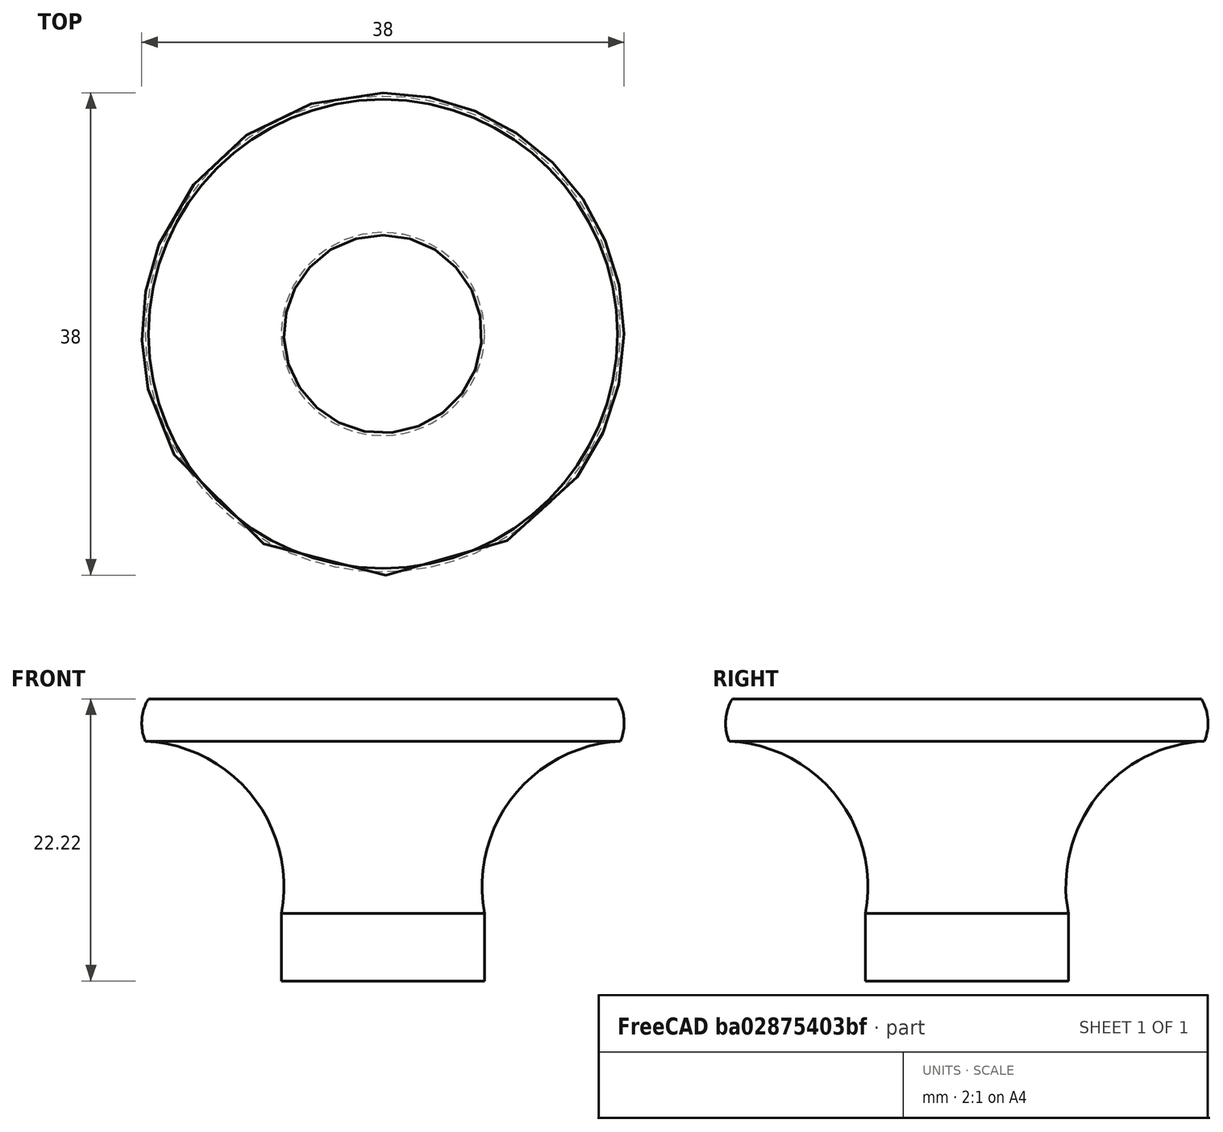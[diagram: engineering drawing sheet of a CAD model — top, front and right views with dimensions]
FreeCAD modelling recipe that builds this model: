
FCSTD DOCUMENT  (FreeCAD 1.1R20260325 (Git shallow))
Label: msf068
License: All rights reserved
LicenseURL: https://en.wikipedia.org/wiki/All_rights_reserved
objects: App::LinkGroup×2, App::Point×2, Sketcher::SketchObject×1, PartDesign::Revolution×1, PartDesign::Body×1, App::Part×1
note: 6 computed .brp shape members not serialized (recipe doc carries the construction recipe); baked Part::Feature solids carry a one-line shape summary decoded from their .brp

FEATURE [Sketcher::SketchObject] Sketch
  ArcFitTolerance = 0
  ExternalTypes = [0]
  FullyConstrained = false
  MakeInternals = false
  MapMode = 5
  Placement = pos=(0,0,0) rot=(0.57735,0.57735,0.57735;2.0944rad)
  _ExternalGeoVersion = 0
  sketch-geometry (8):
    g0: LineSegment StartX=0 StartY=0 StartZ=0 EndX=8 EndY=0 EndZ=0
    g1: LineSegment StartX=8 StartY=0 StartZ=0 EndX=8 EndY=5.33538 EndZ=0
    g2: ArcOfCircle CenterX=19.2411 CenterY=7.45526 CenterZ=0 NormalX=0 NormalY=0 NormalZ=1 AngleXU=0 Radius=11.4392 StartAngle=1.61634 EndAngle=3.32799
    g3: ArcOfCircle CenterX=15.253 CenterY=20.3071 CenterZ=0 NormalX=0 NormalY=0 NormalZ=1 AngleXU=0 Radius=3.74848 StartAngle=5.89336 EndAngle=6.82
    g4: ArcOfCircle CenterX=-1.25475 CenterY=-61.8052 CenterZ=0 NormalX=0 NormalY=0 NormalZ=1 AngleXU=0 Radius=86.3143 StartAngle=1.34019 EndAngle=1.55626
    g5: LineSegment StartX=4.2e-15 StartY=24.5 StartZ=0 EndX=0 EndY=0 EndZ=0
    g6: LineSegment [constr] StartX=19 StartY=0 StartZ=0 EndX=19 EndY=20.4133 EndZ=0
    g7: LineSegment [constr] StartX=4.2e-15 StartY=24.5 StartZ=0 EndX=9.88874e-07 EndY=24.5 EndZ=0
  constraints (17):
    c: Coincident(g0,g-1)
    c: PointOnObject(g0,g-1)
    c: Coincident(g1,g0)
    c: Vertical(g1)
    c: Coincident(g2,g1)
    c: Coincident(g3,g2)
    c: Coincident(g4,g3)
    c: PointOnObject(g4,g-2)
    c: Coincident(g5,g4)
    c: Coincident(g5,g0)
    c: DistanceX(g0,g0) = 8
    c: PointOnObject(g6,g-1)
    c: Vertical(g6)
    c: PointOnObject(g6,g3)
    c: DistanceX(g4,g6) = 19
    c: DistanceY(g0,g7) = 24.5
    c: Tangent(g4,g7) = 1.5708
FEATURE [PartDesign::Revolution] Revolution
  Angle = 360
  Angle2 = 0
  Axis = (1e-16,-1e-16,1)
  Base = (0,0,0)
  FuseOrder = 0
  Placement = pos=(0,0,0) rot=(0.57735,0.57735,0.57735;2.0944rad)
  Profile = -> Sketch
  ReferenceAxis = -> Sketch [V_Axis]
  Reversed = true
  Suppressed = false
  Type = 0
FEATURE [PartDesign::Body] Body
  AllowCompound = true
  Group = -> [Sketch,Revolution]
  Origin = -> Origin001
  Tip = -> Revolution
FEATURE [App::Part] Part
  Group = -> [Body]
  Origin = -> Origin
FEATURE [App::LinkGroup] LinkGroup  label="Cabinet handle, link this"
  ElementList = -> [Part]
  LinkMode = 0
FEATURE [App::LinkGroup] LinkGroup001  label="Cabinet handle, hide this"
  ElementList = -> [LinkGroup]
  LinkMode = 0
FEATURE [App::Point] Origin002  label="Origin"
  Role = Origin
FEATURE [App::Point] Origin003  label="Origin"
  Role = Origin
